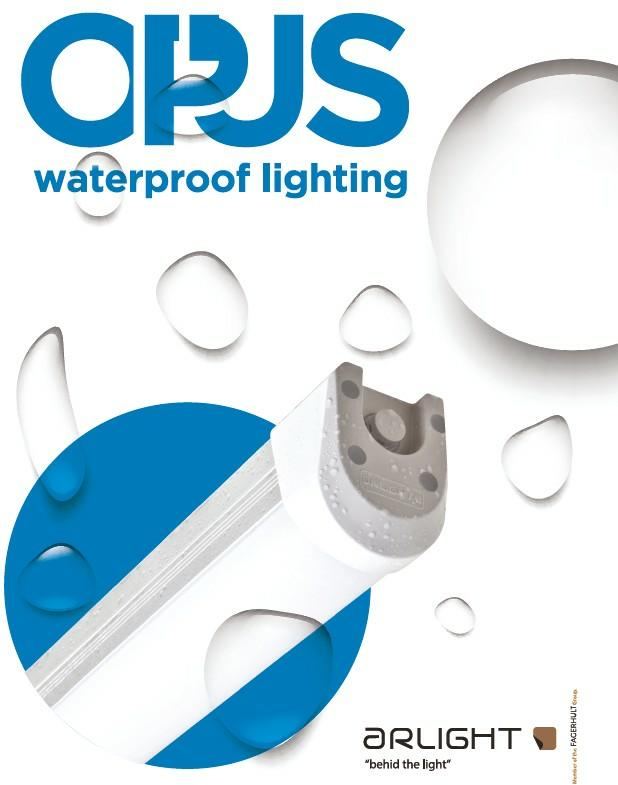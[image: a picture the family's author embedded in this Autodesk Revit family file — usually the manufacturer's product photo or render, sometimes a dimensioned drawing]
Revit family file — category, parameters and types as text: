
# Revit family: E 1200 PUS
name_source: partatom
category: Lighting Fixtures
revit_build: Autodesk Revit 2017 (Build: 20160225_1515(x64)
units: mm (PartAtom-declared; Revit-internal decimal feet)

## family parameters
Cut with Voids When Loaded = No
Host = Face
Light Source = Yes
Part Type = Normal
Room Calculation Point = No
Round Connector Dimension = Use Diameter
Shared = No

## types (8) — shared parameters
Color Filter = 16777215
Default Elevation = 1219 mm
Description = Double Connector
Dimming Lamp Color Temperature Shift = <None>
Emit Shape Visible in Rendering = No
Emit from Rectangle Length = 1138 mm  [stored 3.7336 ft]
Emit from Rectangle Width = 55 mm  [stored 0.180446 ft]
Lamp = LED
Manufacturer = ARLIGHT AYDINLATMA
Model = E 1200 PUS (CK)
Photometric Web File = E 1200 PUS-50W-4K(SK).IES
Tilt Angle = -90.00°
Type Comments = Waterproof Lighting
Type Image = OPUS.jpg
URL = http://www.arlight.net

## per-type parameters (varying)
| type | Apparent Load | Wattage Comments |
| EPUS.1200.34.40.TK | 34 VA | 34W |
| EPUS.1200.49.40.TK | 49 VA | 49W |
| EPUS.1200.34.40.CK | 34 VA | 34W |
| EPUS.1200.49.40.CK | 49 VA | 49W |
| EPUS.1200.34.40.TR | 34 VA | 34W |
| EPUS.1200.49.40.TR | 49 VA | 49W |
| EPUS.1200.34.40.CR | 34 VA | 34W |
| EPUS.1200.49.40.CR | 49 VA | 49W |

note: [stored X ft] marks values corroborated as IEEE doubles in the binary element streams (Revit-internal decimal feet)

## geometry (parser evidence)
native form markers: Sweep x3
no freeform markers — native parametric forms only
